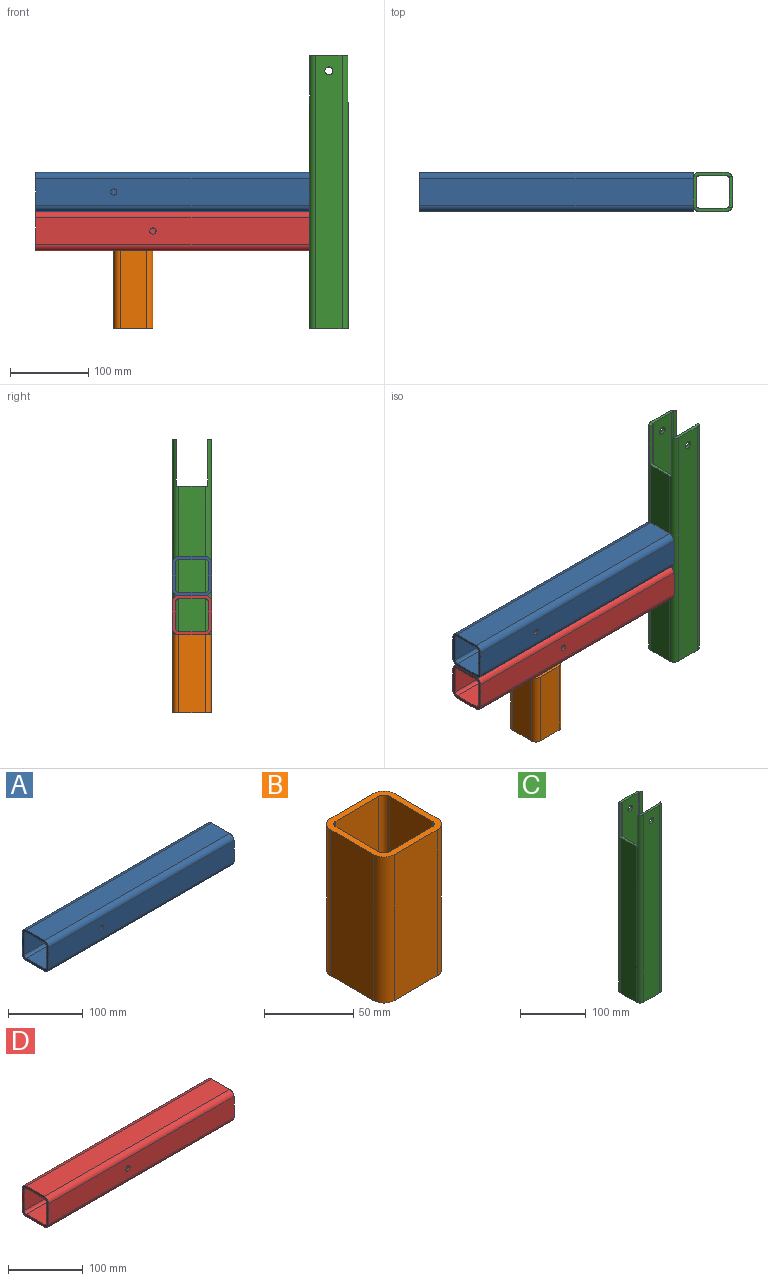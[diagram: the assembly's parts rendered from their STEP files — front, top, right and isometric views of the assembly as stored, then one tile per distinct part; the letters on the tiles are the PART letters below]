
ASSEMBLY  parts=4 mates=3
PART A: 19 faces, bbox 350x50x50 mm
  f0: plane 350x34mm, normal (0,0,-1), area 11900mm2, adj f1,f7,f8,f9
  f1: cylinder r=4mm len=350mm, axis (-1,0,0), area 2199.1mm2, adj f0,f2,f8,f9
  f2: plane 350x34mm, normal (0,1,0), area 11849.7mm2, adj f1,f3,f8,f9,f18
  f3: cylinder r=4mm len=350mm, axis (-1,0,0), area 2199.1mm2, adj f2,f4,f8,f9
  f4: plane 350x34mm, normal (0,0,1), area 11900mm2, adj f3,f5,f8,f9
  f5: cylinder r=4mm len=350mm, axis (-1,0,0), area 2199.1mm2, adj f4,f6,f8,f9
  f6: plane 350x34mm, normal (0,-1,0), area 11900mm2, adj f5,f7,f8,f9
  f7: cylinder r=4mm len=350mm, axis (-1,0,0), area 2199.1mm2, adj f0,f6,f8,f9
  f8: plane 50x50mm, normal (1,0,0), area 694.8mm2, adj f0,f1,f2,f3,f4,f5,f6,f7
  f9: plane 50x50mm, normal (-1,0,0), area 694.8mm2, adj f0,f1,f2,f3,f4,f5,f6,f7
  f10: plane 350x34mm, normal (0,0,-1), area 11900mm2, adj f8,f9,f11,f17
  f11: cylinder r=8mm len=350mm, axis (-1,0,0), area 4398.3mm2, adj f8,f9,f10,f12
  f12: plane 350x34mm, normal (0,-1,0), area 11849.7mm2, adj f8,f9,f11,f13,f18
  f13: cylinder r=8mm len=350mm, axis (-1,0,0), area 4398.3mm2, adj f8,f9,f12,f14
  f14: plane 350x34mm, normal (0,0,1), area 11900mm2, adj f8,f9,f13,f15
  f15: cylinder r=8mm len=350mm, axis (-1,0,0), area 4398.3mm2, adj f8,f9,f14,f16
  f16: plane 350x34mm, normal (0,1,0), area 11900mm2, adj f8,f9,f15,f17
  f17: cylinder r=8mm len=350mm, axis (-1,0,0), area 4398.3mm2, adj f8,f9,f10,f16
  f18: cylinder r=4mm len=8mm, axis (0,-1,0), area 100.5mm2, adj f2,f12
PART B: 18 faces, bbox 50x50x100 mm
  f0: plane 100x34mm, normal (0,1,0), area 3400mm2, adj f1,f7,f8,f9
  f1: cylinder r=4mm len=100mm, axis (0,0,1), area 628.3mm2, adj f0,f2,f8,f9
  f2: plane 100x34mm, normal (1,0,0), area 3400mm2, adj f1,f3,f8,f9
  f3: cylinder r=4mm len=100mm, axis (0,0,1), area 628.3mm2, adj f2,f4,f8,f9
  f4: plane 100x34mm, normal (0,-1,0), area 3400mm2, adj f3,f5,f8,f9
  f5: cylinder r=4mm len=100mm, axis (0,0,1), area 628.3mm2, adj f4,f6,f8,f9
  f6: plane 100x34mm, normal (-1,0,0), area 3400mm2, adj f5,f7,f8,f9
  f7: cylinder r=4mm len=100mm, axis (0,0,1), area 628.3mm2, adj f0,f6,f8,f9
  f8: plane 50x50mm, normal (0,0,-1), area 694.8mm2, adj f0,f1,f2,f3,f4,f5,f6,f7
  f9: plane 50x50mm, normal (0,0,1), area 694.8mm2, adj f0,f1,f2,f3,f4,f5,f6,f7
  f10: plane 100x34mm, normal (0,1,0), area 3400mm2, adj f8,f9,f11,f17
  f11: cylinder r=8mm len=100mm, axis (0,0,1), area 1256.6mm2, adj f8,f9,f10,f12
  f12: plane 100x34mm, normal (-1,0,0), area 3400mm2, adj f8,f9,f11,f13
  f13: cylinder r=8mm len=100mm, axis (0,0,1), area 1256.6mm2, adj f8,f9,f12,f14
  f14: plane 100x34mm, normal (0,-1,0), area 3400mm2, adj f8,f9,f13,f15
  f15: cylinder r=8mm len=100mm, axis (0,0,1), area 1256.6mm2, adj f8,f9,f14,f16
  f16: plane 100x34mm, normal (1,0,0), area 3400mm2, adj f8,f9,f15,f17
  f17: cylinder r=8mm len=100mm, axis (0,0,1), area 1256.6mm2, adj f8,f9,f10,f16
PART C: 27 faces, bbox 50x50x350 mm
  f0: plane 290x34mm, normal (1,0,0), area 9860mm2, adj f11,f12,f15,f20
  f1: cylinder r=4mm len=350mm, axis (0,0,1), area 1995.6mm2, adj f2,f7,f13,f15,f22,f23
  f2: plane 290x34mm, normal (1,0,0), area 9860mm2, adj f1,f3,f15,f23
  f3: cylinder r=4mm len=350mm, axis (0,0,1), area 1995.6mm2, adj f2,f14,f15,f16,f23,f24
  f4: cylinder r=4mm len=350mm, axis (0,0,1), area 1995.6mm2, adj f5,f14,f15,f16,f19,f20
  f5: plane 290x34mm, normal (-1,0,0), area 9860mm2, adj f4,f6,f15,f20
  f6: cylinder r=4mm len=350mm, axis (0,0,1), area 1995.6mm2, adj f5,f7,f13,f15,f20,f21
  f7: plane 48.83x5mm, normal (0,0,1), area 186.1mm2, adj f1,f6,f10,f11,f13,f18,f21,f22
  f8: cylinder r=8mm len=350mm, axis (0,0,1), area 4213.7mm2, adj f9,f15,f16,f17,f23,f24
  f9: plane 290x34mm, normal (-1,0,0), area 9860mm2, adj f8,f10,f15,f23
  f10: cylinder r=8mm len=350mm, axis (0,0,1), area 4213.7mm2, adj f7,f9,f15,f18,f22,f23
  f11: cylinder r=8mm len=350mm, axis (0,0,1), area 4213.7mm2, adj f0,f7,f15,f18,f20,f21
  f12: cylinder r=8mm len=350mm, axis (0,0,1), area 4213.7mm2, adj f0,f15,f16,f17,f19,f20
  f13: plane 350x34mm, normal (0,1,0), area 11821.5mm2, adj f1,f6,f7,f15,f25
  f14: plane 350x34mm, normal (0,-1,0), area 11821.5mm2, adj f3,f4,f15,f16,f26
  f15: plane 50x50mm, normal (0,0,-1), area 694.8mm2, adj f0,f1,f2,f3,f4,f5,f6,f8
  f16: plane 48.83x5mm, normal (0,0,1), area 186.1mm2, adj f3,f4,f8,f12,f14,f17,f19,f24
  f17: plane 350x34mm, normal (0,1,0), area 11821.5mm2, adj f8,f12,f15,f16,f26
  f18: plane 350x34mm, normal (0,-1,0), area 11821.5mm2, adj f7,f10,f11,f15,f25
  f19: plane 60x4.77mm, normal (0,-1,0), area 286.2mm2, adj f4,f12,f16,f20
  f20: plane 40x5.35mm, normal (0,0,1), area 161.3mm2, adj f0,f4,f5,f6,f11,f12,f19,f21
  f21: plane 60x4.77mm, normal (0,1,0), area 286.2mm2, adj f6,f7,f11,f20
  f22: plane 60x4.77mm, normal (0,1,0), area 286.2mm2, adj f1,f7,f10,f23
  f23: plane 40x5.35mm, normal (0,0,1), area 161.3mm2, adj f1,f2,f3,f8,f9,f10,f22,f24
  f24: plane 60x4.77mm, normal (0,-1,0), area 286.2mm2, adj f3,f8,f16,f23
  f25: cylinder r=5mm len=10mm, axis (0,-1,0), area 125.7mm2, adj f13,f18
  f26: cylinder r=5mm len=10mm, axis (0,-1,0), area 125.7mm2, adj f14,f17
PART D: 19 faces, bbox 350x50x50 mm
  f0: plane 350x34mm, normal (0,0,-1), area 11900mm2, adj f1,f7,f8,f9
  f1: cylinder r=4mm len=350mm, axis (-1,0,0), area 2199.1mm2, adj f0,f2,f8,f9
  f2: plane 350x34mm, normal (0,1,0), area 11849.7mm2, adj f1,f3,f8,f9,f18
  f3: cylinder r=4mm len=350mm, axis (-1,0,0), area 2199.1mm2, adj f2,f4,f8,f9
  f4: plane 350x34mm, normal (0,0,1), area 11900mm2, adj f3,f5,f8,f9
  f5: cylinder r=4mm len=350mm, axis (-1,0,0), area 2199.1mm2, adj f4,f6,f8,f9
  f6: plane 350x34mm, normal (0,-1,0), area 11900mm2, adj f5,f7,f8,f9
  f7: cylinder r=4mm len=350mm, axis (-1,0,0), area 2199.1mm2, adj f0,f6,f8,f9
  f8: plane 50x50mm, normal (1,0,0), area 694.8mm2, adj f0,f1,f2,f3,f4,f5,f6,f7
  f9: plane 50x50mm, normal (-1,0,0), area 694.8mm2, adj f0,f1,f2,f3,f4,f5,f6,f7
  f10: plane 350x34mm, normal (0,0,-1), area 11900mm2, adj f8,f9,f11,f17
  f11: cylinder r=8mm len=350mm, axis (-1,0,0), area 4398.3mm2, adj f8,f9,f10,f12
  f12: plane 350x34mm, normal (0,-1,0), area 11849.7mm2, adj f8,f9,f11,f13,f18
  f13: cylinder r=8mm len=350mm, axis (-1,0,0), area 4398.3mm2, adj f8,f9,f12,f14
  f14: plane 350x34mm, normal (0,0,1), area 11900mm2, adj f8,f9,f13,f15
  f15: cylinder r=8mm len=350mm, axis (-1,0,0), area 4398.3mm2, adj f8,f9,f14,f16
  f16: plane 350x34mm, normal (0,1,0), area 11900mm2, adj f8,f9,f15,f17
  f17: cylinder r=8mm len=350mm, axis (-1,0,0), area 4398.3mm2, adj f8,f9,f10,f16
  f18: cylinder r=4mm len=8mm, axis (0,-1,0), area 100.5mm2, adj f2,f12
PLACE A t=(-25,0,175)mm
PLACE B t=(-250,0,0)mm
PLACE C at identity fixed
PLACE D t=(-25,0,125)mm
MATE fastened D.f8 <-> C.f9  axis (1,0,0) through (-25,0,100)mm
MATE fastened A.f10 <-> D.f14  axis (0,0,-1) through (-200,0,150)mm
MATE fastened B.f9 <-> D.f10  axis (0,0,1) through (-275,0,100)mm
